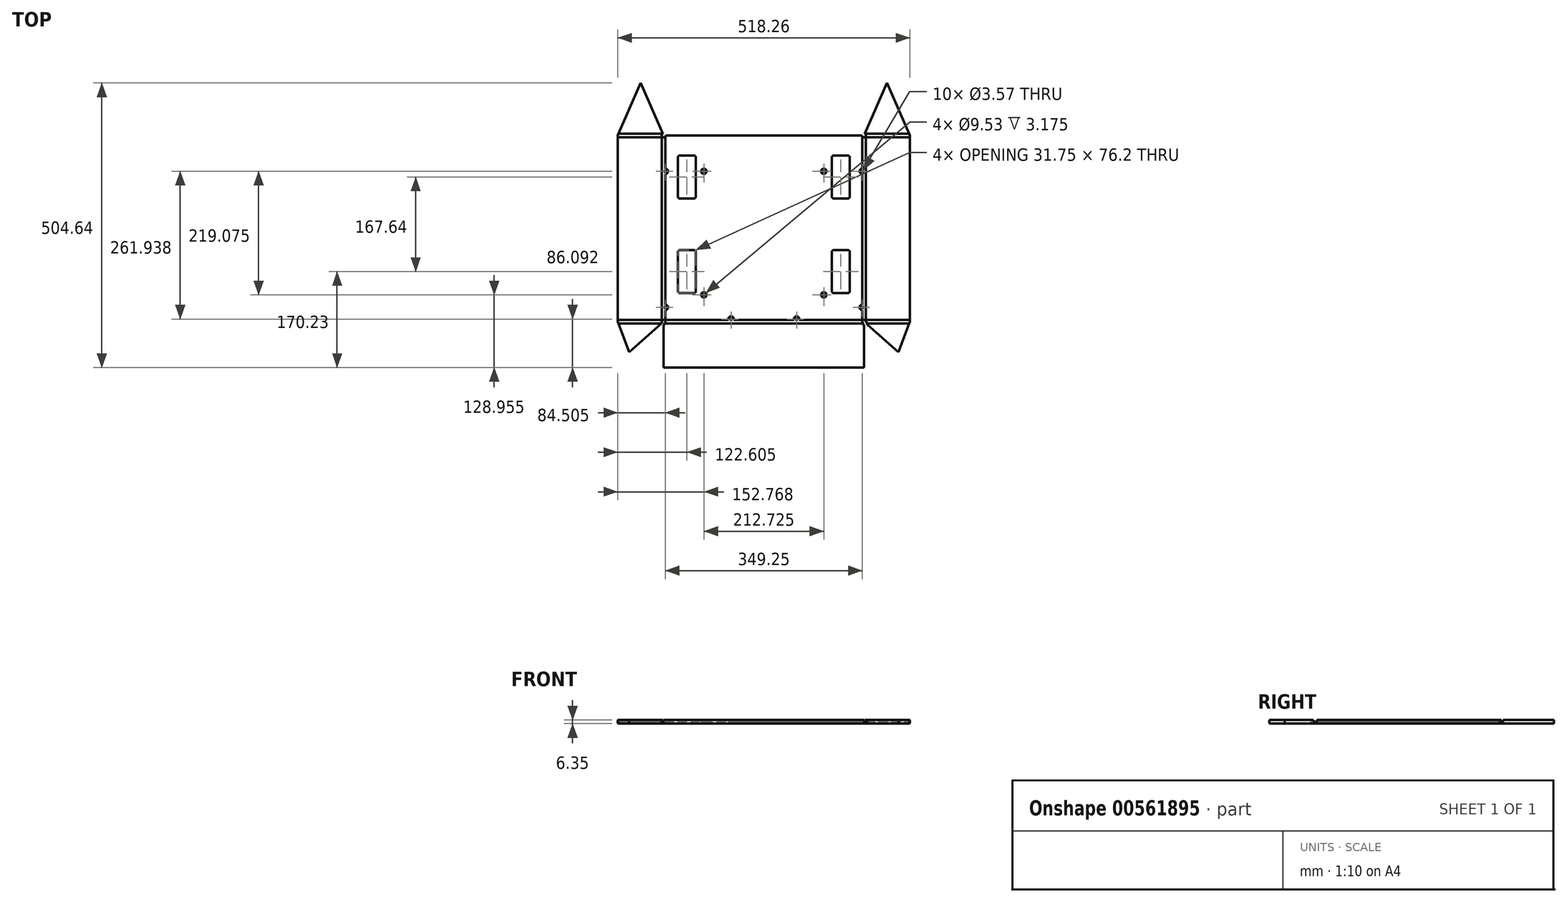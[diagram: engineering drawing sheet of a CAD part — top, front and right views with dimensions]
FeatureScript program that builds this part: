
annotation { "Feature Type Name" : "Feature", "Feature Type Description" : "" }
export const myFeature = defineFeature(function(context is Context, id is Id, definition is map)
    precondition{}
    {
        {
            var Q0;
            Q0=qCreatedBy(makeId("Top.planeOp"),FACE);
            var sketch = newSketch(context, id + "F0", { "sketchPlane" : qUnion([Q0])});
            skLineSegment(sketch, "E0", {"start": v(-255.4, 111.76) * mm, "end": v(-255.4, -218.44) * mm});
            skLineSegment(sketch, "E1", {"start": v(-255.4, -218.44) * mm, "end": v(-234.78, -272.56) * mm});
            skLineSegment(sketch, "E2", {"start": v(-234.78, -272.56) * mm, "end": v(-174.07, -218.44) * mm});
            skLineSegment(sketch, "E3", {"start": v(-174.07, -218.44) * mm, "end": v(-174.07, -299.77) * mm});
            skLineSegment(sketch, "E4", {"start": v(-174.07, -218.44) * mm, "end": v(-174.07, 111.76) * mm, "construction": true});
            skLineSegment(sketch, "E5", {"start": v(-174.07, -218.44) * mm, "end": v(-255.4, -218.44) * mm, "construction": true});
            skLineSegment(sketch, "E6", {"start": v(-174.07, -299.77) * mm, "end": v(181.53, -299.77) * mm});
            skLineSegment(sketch, "E7", {"start": v(181.53, -299.77) * mm, "end": v(181.53, -218.44) * mm});
            skLineSegment(sketch, "E8", {"start": v(181.53, -218.44) * mm, "end": v(242.24, -272.56) * mm});
            skLineSegment(sketch, "E9", {"start": v(242.24, -272.56) * mm, "end": v(262.86, -218.44) * mm});
            skLineSegment(sketch, "E10", {"start": v(181.53, -218.44) * mm, "end": v(262.86, -218.44) * mm, "construction": true});
            skLineSegment(sketch, "E11", {"start": v(-174.07, 111.76) * mm, "end": v(-255.4, 111.76) * mm, "construction": true});
            skLineSegment(sketch, "E12", {"start": v(262.86, -218.44) * mm, "end": v(262.86, 111.76) * mm});
            skLineSegment(sketch, "E13", {"start": v(262.86, 111.76) * mm, "end": v(181.53, 111.76) * mm, "construction": true});
            skLineSegment(sketch, "E14", {"start": v(181.53, 111.76) * mm, "end": v(181.53, -218.44) * mm, "construction": true});
            skLineSegment(sketch, "E15", {"start": v(-255.4, 111.76) * mm, "end": v(-214.74, 204.87) * mm});
            skLineSegment(sketch, "E16", {"start": v(-214.74, 204.87) * mm, "end": v(-174.07, 111.76) * mm});
            skLineSegment(sketch, "E17", {"start": v(181.53, 111.76) * mm, "end": v(222.2, 204.87) * mm});
            skLineSegment(sketch, "E18", {"start": v(222.2, 204.87) * mm, "end": v(262.86, 111.76) * mm});
            skCircle(sketch, "E19", {"center": v(-174.07, -218.44) * mm, "radius": 3.18 * mm});
            skLineSegment(sketch, "E20", {"start": v(-174.62, -215.31) * mm, "end": v(-177.5, -221.5) * mm});
            skLineSegment(sketch, "E21", {"start": v(-171.2, -219.78) * mm, "end": v(-174.07, -225.97) * mm});
            skCircle(sketch, "E22", {"center": v(181.53, -218.44) * mm, "radius": 3.18 * mm});
            skLineSegment(sketch, "E23", {"start": v(178.63, -219.74) * mm, "end": v(181.53, -226.2) * mm});
            skLineSegment(sketch, "E24", {"start": v(184.43, -217.14) * mm, "end": v(187.32, -223.6) * mm});
            skLineSegment(sketch, "E25", {"start": v(-174.07, 111.76) * mm, "end": v(181.53, 111.76) * mm});
            skCircle(sketch, "E26", {"center": v(-174.07, 111.76) * mm, "radius": 3.18 * mm});
            skLineSegment(sketch, "E27", {"start": v(-171.41, 110.02) * mm, "end": v(-170.28, 111.76) * mm});
            skLineSegment(sketch, "E28", {"start": v(-176.73, 113.5) * mm, "end": v(-175.59, 115.24) * mm});
            skCircle(sketch, "E29", {"center": v(181.53, 111.76) * mm, "radius": 3.18 * mm});
            skLineSegment(sketch, "E30", {"start": v(178.87, 110.02) * mm, "end": v(177.74, 111.76) * mm});
            skLineSegment(sketch, "E31", {"start": v(184.19, 113.5) * mm, "end": v(183.05, 115.24) * mm});
            skLineSegment(sketch, "E32", {"start": v(-174.07, -218.44) * mm, "end": v(181.53, -218.44) * mm, "construction": true});
            skLineSegment(sketch, "E33", {"start": v(-148.67, 111.76) * mm, "end": v(-148.67, -218.44) * mm, "construction": true});
            skLineSegment(sketch, "E34", {"start": v(156.13, 111.76) * mm, "end": v(156.13, -218.44) * mm, "construction": true});
            skLineSegment(sketch, "E35", {"start": v(-116.92, 111.76) * mm, "end": v(-116.92, -218.44) * mm, "construction": true});
            skLineSegment(sketch, "E36", {"start": v(124.38, 111.76) * mm, "end": v(124.38, -218.44) * mm, "construction": true});
            skLineSegment(sketch, "E37", {"start": v(-174.07, 76.2) * mm, "end": v(181.53, 76.2) * mm, "construction": true});
            skLineSegment(sketch, "E38", {"start": v(-174.07, 0) * mm, "end": v(181.53, 0) * mm, "construction": true});
            skLineSegment(sketch, "E39", {"start": v(-174.07, -167.64) * mm, "end": v(181.53, -167.64) * mm, "construction": true});
            skLineSegment(sketch, "E40", {"start": v(-174.07, -91.44) * mm, "end": v(181.53, -91.44) * mm, "construction": true});
            skLineSegment(sketch, "E41.bottom", {"start": v(-148.67, 76.2) * mm, "end": v(-116.92, 76.2) * mm});
            skLineSegment(sketch, "E41.top", {"start": v(-148.67, 0) * mm, "end": v(-116.92, 0) * mm});
            skLineSegment(sketch, "E41.left", {"start": v(-148.67, 76.2) * mm, "end": v(-148.67, 0) * mm});
            skLineSegment(sketch, "E41.right", {"start": v(-116.92, 76.2) * mm, "end": v(-116.92, 0) * mm});
            skLineSegment(sketch, "E42.bottom", {"start": v(124.38, 76.2) * mm, "end": v(156.13, 76.2) * mm});
            skLineSegment(sketch, "E42.top", {"start": v(124.38, 0) * mm, "end": v(156.13, 0) * mm});
            skLineSegment(sketch, "E42.left", {"start": v(124.38, 76.2) * mm, "end": v(124.38, 0) * mm});
            skLineSegment(sketch, "E42.right", {"start": v(156.13, 76.2) * mm, "end": v(156.13, 0) * mm});
            skLineSegment(sketch, "E43.bottom", {"start": v(156.13, -91.44) * mm, "end": v(124.38, -91.44) * mm});
            skLineSegment(sketch, "E43.top", {"start": v(156.13, -167.64) * mm, "end": v(124.38, -167.64) * mm});
            skLineSegment(sketch, "E43.left", {"start": v(156.13, -91.44) * mm, "end": v(156.13, -167.64) * mm});
            skLineSegment(sketch, "E43.right", {"start": v(124.38, -91.44) * mm, "end": v(124.38, -167.64) * mm});
            skLineSegment(sketch, "E44.bottom", {"start": v(-116.92, -91.44) * mm, "end": v(-148.67, -91.44) * mm});
            skLineSegment(sketch, "E44.top", {"start": v(-116.92, -167.64) * mm, "end": v(-148.67, -167.64) * mm});
            skLineSegment(sketch, "E44.left", {"start": v(-116.92, -91.44) * mm, "end": v(-116.92, -167.64) * mm});
            skLineSegment(sketch, "E44.right", {"start": v(-148.67, -91.44) * mm, "end": v(-148.67, -167.64) * mm});
            skLineSegment(sketch, "E45", {"start": v(-170.9, 111.76) * mm, "end": v(-170.9, 48.26) * mm, "construction": true});
            skLineSegment(sketch, "E46", {"start": v(-170.9, -218.44) * mm, "end": v(-170.9, -193.04) * mm, "construction": true});
            skLineSegment(sketch, "E47", {"start": v(178.36, -218.44) * mm, "end": v(178.36, -193.04) * mm, "construction": true});
            skLineSegment(sketch, "E48", {"start": v(178.36, 111.76) * mm, "end": v(178.36, 48.26) * mm, "construction": true});
            skLineSegment(sketch, "E49", {"start": v(178.36, 48.26) * mm, "end": v(110.1, 48.26) * mm, "construction": true});
            skLineSegment(sketch, "E50", {"start": v(-170.9, 48.26) * mm, "end": v(-102.63, 48.26) * mm, "construction": true});
            skPoint(sketch, "E51", {"position": v(-102.63, 48.26) * mm});
            skPoint(sketch, "E52", {"position": v(-102.63, -170.82) * mm});
            skPoint(sketch, "E53", {"position": v(110.1, -170.81) * mm});
            skPoint(sketch, "E54", {"position": v(110.1, 48.26) * mm});
            skLineSegment(sketch, "E55", {"start": v(-174.07, -213.68) * mm, "end": v(181.53, -213.68) * mm, "construction": true});
            skPoint(sketch, "E56", {"position": v(61.83, -213.68) * mm});
            skPoint(sketch, "E57", {"position": v(-54.37, -213.68) * mm});
            skLineSegment(sketch, "E58", {"start": v(-102.63, -170.82) * mm, "end": v(-102.63, -218.44) * mm, "construction": true});
            skLineSegment(sketch, "E59", {"start": v(110.1, -170.81) * mm, "end": v(110.1, -218.44) * mm, "construction": true});
            skSolve(sketch);
        }
        {
            var Q0;
            Q0=makeQuery(id+"F0.imprint","IMPRINT",FACE,{"disambiguationData":[TD([[makeQuery(id+"F0.imprint","IMPRINT",EDGE,{"derivedFrom":sQuery(id+"F0.wireOp",EDGE,"E0")}),1.0]])]});
            extrude(context, id + "F1", {"entities" : qUnion([Q0]), "depth" : 6.35 * mm});
        }
        {
            var Q0;
            Q0=makeQuery(id+"F1.opExtrude","SWEPT_EDGE",EDGE,{"disambiguationData":[OSD([sQuery(id+"F0.wireOp",EDGE,"E42.bottom"),sQuery(id+"F0.wireOp",EDGE,"E42.right")])]});
            var Q1;
            Q1=makeQuery(id+"F1.opExtrude","SWEPT_EDGE",EDGE,{"disambiguationData":[OSD([sQuery(id+"F0.wireOp",EDGE,"E42.bottom"),sQuery(id+"F0.wireOp",EDGE,"E42.left")])]});
            var Q2;
            Q2=makeQuery(id+"F1.opExtrude","SWEPT_EDGE",EDGE,{"disambiguationData":[OSD([sQuery(id+"F0.wireOp",EDGE,"E42.top"),sQuery(id+"F0.wireOp",EDGE,"E42.left")])]});
            var Q3;
            Q3=makeQuery(id+"F1.opExtrude","SWEPT_EDGE",EDGE,{"disambiguationData":[OSD([sQuery(id+"F0.wireOp",EDGE,"E42.top"),sQuery(id+"F0.wireOp",EDGE,"E42.right")])]});
            var Q4;
            Q4=makeQuery(id+"F1.opExtrude","SWEPT_EDGE",EDGE,{"disambiguationData":[OSD([sQuery(id+"F0.wireOp",EDGE,"E43.top"),sQuery(id+"F0.wireOp",EDGE,"E43.left")])]});
            var Q5;
            Q5=makeQuery(id+"F1.opExtrude","SWEPT_EDGE",EDGE,{"disambiguationData":[OSD([sQuery(id+"F0.wireOp",EDGE,"E43.top"),sQuery(id+"F0.wireOp",EDGE,"E43.right")])]});
            var Q6;
            Q6=makeQuery(id+"F1.opExtrude","SWEPT_EDGE",EDGE,{"disambiguationData":[OSD([sQuery(id+"F0.wireOp",EDGE,"E43.bottom"),sQuery(id+"F0.wireOp",EDGE,"E43.right")])]});
            var Q7;
            Q7=makeQuery(id+"F1.opExtrude","SWEPT_EDGE",EDGE,{"disambiguationData":[OSD([sQuery(id+"F0.wireOp",EDGE,"E43.bottom"),sQuery(id+"F0.wireOp",EDGE,"E43.left")])]});
            var Q8;
            Q8=makeQuery(id+"F1.opExtrude","SWEPT_EDGE",EDGE,{"disambiguationData":[OSD([sQuery(id+"F0.wireOp",EDGE,"E44.bottom"),sQuery(id+"F0.wireOp",EDGE,"E44.left")])]});
            var Q9;
            Q9=makeQuery(id+"F1.opExtrude","SWEPT_EDGE",EDGE,{"disambiguationData":[OSD([sQuery(id+"F0.wireOp",EDGE,"E44.top"),sQuery(id+"F0.wireOp",EDGE,"E44.left")])]});
            var Q10;
            Q10=makeQuery(id+"F1.opExtrude","SWEPT_EDGE",EDGE,{"disambiguationData":[OSD([sQuery(id+"F0.wireOp",EDGE,"E41.top"),sQuery(id+"F0.wireOp",EDGE,"E41.right")])]});
            var Q11;
            Q11=makeQuery(id+"F1.opExtrude","SWEPT_EDGE",EDGE,{"disambiguationData":[OSD([sQuery(id+"F0.wireOp",EDGE,"E44.top"),sQuery(id+"F0.wireOp",EDGE,"E44.right")])]});
            var Q12;
            Q12=makeQuery(id+"F1.opExtrude","SWEPT_EDGE",EDGE,{"disambiguationData":[OSD([sQuery(id+"F0.wireOp",EDGE,"E41.top"),sQuery(id+"F0.wireOp",EDGE,"E41.left")])]});
            var Q13;
            Q13=makeQuery(id+"F1.opExtrude","SWEPT_EDGE",EDGE,{"disambiguationData":[OSD([sQuery(id+"F0.wireOp",EDGE,"E44.bottom"),sQuery(id+"F0.wireOp",EDGE,"E44.right")])]});
            var Q14;
            Q14=makeQuery(id+"F1.opExtrude","SWEPT_EDGE",EDGE,{"disambiguationData":[OSD([sQuery(id+"F0.wireOp",EDGE,"E41.bottom"),sQuery(id+"F0.wireOp",EDGE,"E41.left")])]});
            var Q15;
            Q15=makeQuery(id+"F1.opExtrude","SWEPT_EDGE",EDGE,{"disambiguationData":[OSD([sQuery(id+"F0.wireOp",EDGE,"E41.bottom"),sQuery(id+"F0.wireOp",EDGE,"E41.right")])]});
            fillet(context, id + "F2", {"entities" : qUnion([Q0, Q1, Q2, Q3, Q4, Q5, Q6, Q7, Q8, Q9, Q10, Q11, Q12, Q13, Q14, Q15]), "radius" : 3.17 * mm, "tangentPropagation" : true, "allowEdgeOverflow" : false});
        }
        {
            var Q0;
            Q0=sQuery(id+"F0.wireOp",VERTEX,"E48.end");
            var Q1;
            Q1=makeQuery(id+"F1.opExtrude","SWEPT_BODY",BODY,{"disambiguationData":[OSD([sQuery(id+"F0.wireOp",EDGE,"E0"),sQuery(id+"F0.wireOp",EDGE,"E1"),sQuery(id+"F0.wireOp",EDGE,"E2"),sQuery(id+"F0.wireOp",EDGE,"E3"),sQuery(id+"F0.wireOp",EDGE,"E6"),sQuery(id+"F0.wireOp",EDGE,"E7"),sQuery(id+"F0.wireOp",EDGE,"E8"),sQuery(id+"F0.wireOp",EDGE,"E9"),sQuery(id+"F0.wireOp",EDGE,"E12"),sQuery(id+"F0.wireOp",EDGE,"E15"),sQuery(id+"F0.wireOp",EDGE,"E16"),sQuery(id+"F0.wireOp",EDGE,"E17"),sQuery(id+"F0.wireOp",EDGE,"E18"),sQuery(id+"F0.wireOp",EDGE,"E19"),sQuery(id+"F0.wireOp",EDGE,"E20"),sQuery(id+"F0.wireOp",EDGE,"E21"),sQuery(id+"F0.wireOp",EDGE,"E22"),sQuery(id+"F0.wireOp",EDGE,"E23"),sQuery(id+"F0.wireOp",EDGE,"E24"),sQuery(id+"F0.wireOp",EDGE,"E25"),sQuery(id+"F0.wireOp",EDGE,"E26"),sQuery(id+"F0.wireOp",EDGE,"E27"),sQuery(id+"F0.wireOp",EDGE,"E28"),sQuery(id+"F0.wireOp",EDGE,"E29"),sQuery(id+"F0.wireOp",EDGE,"E30"),sQuery(id+"F0.wireOp",EDGE,"E31"),sQuery(id+"F0.wireOp",EDGE,"E41.bottom"),sQuery(id+"F0.wireOp",EDGE,"E41.top"),sQuery(id+"F0.wireOp",EDGE,"E41.left"),sQuery(id+"F0.wireOp",EDGE,"E41.right"),sQuery(id+"F0.wireOp",EDGE,"E42.bottom"),sQuery(id+"F0.wireOp",EDGE,"E42.top"),sQuery(id+"F0.wireOp",EDGE,"E42.left"),sQuery(id+"F0.wireOp",EDGE,"E42.right"),sQuery(id+"F0.wireOp",EDGE,"E43.bottom"),sQuery(id+"F0.wireOp",EDGE,"E43.top"),sQuery(id+"F0.wireOp",EDGE,"E43.left"),sQuery(id+"F0.wireOp",EDGE,"E43.right"),sQuery(id+"F0.wireOp",EDGE,"E44.bottom"),sQuery(id+"F0.wireOp",EDGE,"E44.top"),sQuery(id+"F0.wireOp",EDGE,"E44.left"),sQuery(id+"F0.wireOp",EDGE,"E44.right")])]});
            hole(context, id + "F3", {"style" : HoleStyle.SIMPLE, "endStyle" : HoleEndStyle.BLIND, "oppositeDirection" : true, "holeDiameter" : 3.57 * mm, "majorDiameter" : 6.35 * mm, "holeDepth" : 6.35 * mm, "isTappedThrough" : true, "tappedDepth" : 12.7 * mm, "tapClearance" : 3, "startFromSketch" : true, "locations" : qUnion([Q0]), "scope" : qUnion([Q1])});
        }
        {
            var Q0;
            Q0=sQuery(id+"F0.wireOp",VERTEX,"E47.end");
            var Q1;
            Q1=makeQuery(id+"F1.opExtrude","SWEPT_BODY",BODY,{"disambiguationData":[OSD([sQuery(id+"F0.wireOp",EDGE,"E0"),sQuery(id+"F0.wireOp",EDGE,"E1"),sQuery(id+"F0.wireOp",EDGE,"E2"),sQuery(id+"F0.wireOp",EDGE,"E3"),sQuery(id+"F0.wireOp",EDGE,"E6"),sQuery(id+"F0.wireOp",EDGE,"E7"),sQuery(id+"F0.wireOp",EDGE,"E8"),sQuery(id+"F0.wireOp",EDGE,"E9"),sQuery(id+"F0.wireOp",EDGE,"E12"),sQuery(id+"F0.wireOp",EDGE,"E15"),sQuery(id+"F0.wireOp",EDGE,"E16"),sQuery(id+"F0.wireOp",EDGE,"E17"),sQuery(id+"F0.wireOp",EDGE,"E18"),sQuery(id+"F0.wireOp",EDGE,"E19"),sQuery(id+"F0.wireOp",EDGE,"E20"),sQuery(id+"F0.wireOp",EDGE,"E21"),sQuery(id+"F0.wireOp",EDGE,"E22"),sQuery(id+"F0.wireOp",EDGE,"E23"),sQuery(id+"F0.wireOp",EDGE,"E24"),sQuery(id+"F0.wireOp",EDGE,"E25"),sQuery(id+"F0.wireOp",EDGE,"E26"),sQuery(id+"F0.wireOp",EDGE,"E27"),sQuery(id+"F0.wireOp",EDGE,"E28"),sQuery(id+"F0.wireOp",EDGE,"E29"),sQuery(id+"F0.wireOp",EDGE,"E30"),sQuery(id+"F0.wireOp",EDGE,"E31"),sQuery(id+"F0.wireOp",EDGE,"E41.bottom"),sQuery(id+"F0.wireOp",EDGE,"E41.top"),sQuery(id+"F0.wireOp",EDGE,"E41.left"),sQuery(id+"F0.wireOp",EDGE,"E41.right"),sQuery(id+"F0.wireOp",EDGE,"E42.bottom"),sQuery(id+"F0.wireOp",EDGE,"E42.top"),sQuery(id+"F0.wireOp",EDGE,"E42.left"),sQuery(id+"F0.wireOp",EDGE,"E42.right"),sQuery(id+"F0.wireOp",EDGE,"E43.bottom"),sQuery(id+"F0.wireOp",EDGE,"E43.top"),sQuery(id+"F0.wireOp",EDGE,"E43.left"),sQuery(id+"F0.wireOp",EDGE,"E43.right"),sQuery(id+"F0.wireOp",EDGE,"E44.bottom"),sQuery(id+"F0.wireOp",EDGE,"E44.top"),sQuery(id+"F0.wireOp",EDGE,"E44.left"),sQuery(id+"F0.wireOp",EDGE,"E44.right")])]});
            hole(context, id + "F4", {"style" : HoleStyle.SIMPLE, "endStyle" : HoleEndStyle.BLIND, "oppositeDirection" : true, "holeDiameter" : 3.57 * mm, "majorDiameter" : 6.35 * mm, "holeDepth" : 6.35 * mm, "isTappedThrough" : true, "tappedDepth" : 12.7 * mm, "tapClearance" : 3, "startFromSketch" : true, "locations" : qUnion([Q0]), "scope" : qUnion([Q1])});
        }
        {
            var Q0;
            Q0=sQuery(id+"F0.wireOp",VERTEX,"E46.end");
            var Q1;
            Q1=makeQuery(id+"F1.opExtrude","SWEPT_BODY",BODY,{"disambiguationData":[OSD([sQuery(id+"F0.wireOp",EDGE,"E0"),sQuery(id+"F0.wireOp",EDGE,"E1"),sQuery(id+"F0.wireOp",EDGE,"E2"),sQuery(id+"F0.wireOp",EDGE,"E3"),sQuery(id+"F0.wireOp",EDGE,"E6"),sQuery(id+"F0.wireOp",EDGE,"E7"),sQuery(id+"F0.wireOp",EDGE,"E8"),sQuery(id+"F0.wireOp",EDGE,"E9"),sQuery(id+"F0.wireOp",EDGE,"E12"),sQuery(id+"F0.wireOp",EDGE,"E15"),sQuery(id+"F0.wireOp",EDGE,"E16"),sQuery(id+"F0.wireOp",EDGE,"E17"),sQuery(id+"F0.wireOp",EDGE,"E18"),sQuery(id+"F0.wireOp",EDGE,"E19"),sQuery(id+"F0.wireOp",EDGE,"E20"),sQuery(id+"F0.wireOp",EDGE,"E21"),sQuery(id+"F0.wireOp",EDGE,"E22"),sQuery(id+"F0.wireOp",EDGE,"E23"),sQuery(id+"F0.wireOp",EDGE,"E24"),sQuery(id+"F0.wireOp",EDGE,"E25"),sQuery(id+"F0.wireOp",EDGE,"E26"),sQuery(id+"F0.wireOp",EDGE,"E27"),sQuery(id+"F0.wireOp",EDGE,"E28"),sQuery(id+"F0.wireOp",EDGE,"E29"),sQuery(id+"F0.wireOp",EDGE,"E30"),sQuery(id+"F0.wireOp",EDGE,"E31"),sQuery(id+"F0.wireOp",EDGE,"E41.bottom"),sQuery(id+"F0.wireOp",EDGE,"E41.top"),sQuery(id+"F0.wireOp",EDGE,"E41.left"),sQuery(id+"F0.wireOp",EDGE,"E41.right"),sQuery(id+"F0.wireOp",EDGE,"E42.bottom"),sQuery(id+"F0.wireOp",EDGE,"E42.top"),sQuery(id+"F0.wireOp",EDGE,"E42.left"),sQuery(id+"F0.wireOp",EDGE,"E42.right"),sQuery(id+"F0.wireOp",EDGE,"E43.bottom"),sQuery(id+"F0.wireOp",EDGE,"E43.top"),sQuery(id+"F0.wireOp",EDGE,"E43.left"),sQuery(id+"F0.wireOp",EDGE,"E43.right"),sQuery(id+"F0.wireOp",EDGE,"E44.bottom"),sQuery(id+"F0.wireOp",EDGE,"E44.top"),sQuery(id+"F0.wireOp",EDGE,"E44.left"),sQuery(id+"F0.wireOp",EDGE,"E44.right")])]});
            hole(context, id + "F5", {"style" : HoleStyle.SIMPLE, "endStyle" : HoleEndStyle.BLIND, "oppositeDirection" : true, "holeDiameter" : 3.57 * mm, "majorDiameter" : 6.35 * mm, "holeDepth" : 6.35 * mm, "isTappedThrough" : true, "tappedDepth" : 12.7 * mm, "tapClearance" : 3, "startFromSketch" : true, "locations" : qUnion([Q0]), "scope" : qUnion([Q1])});
        }
        {
            var Q0;
            Q0=sQuery(id+"F0.wireOp",VERTEX,"E45.end");
            var Q1;
            Q1=sQuery(id+"F0.wireOp",VERTEX,"E51");
            var Q2;
            Q2=sQuery(id+"F0.wireOp",VERTEX,"E54");
            var Q3;
            Q3=sQuery(id+"F0.wireOp",VERTEX,"E53");
            var Q4;
            Q4=sQuery(id+"F0.wireOp",VERTEX,"E52");
            var Q5;
            Q5=sQuery(id+"F0.wireOp",VERTEX,"E57");
            var Q6;
            Q6=sQuery(id+"F0.wireOp",VERTEX,"E56");
            var Q7;
            Q7=makeQuery(id+"F1.opExtrude","SWEPT_BODY",BODY,{"disambiguationData":[OSD([sQuery(id+"F0.wireOp",EDGE,"E0"),sQuery(id+"F0.wireOp",EDGE,"E1"),sQuery(id+"F0.wireOp",EDGE,"E2"),sQuery(id+"F0.wireOp",EDGE,"E3"),sQuery(id+"F0.wireOp",EDGE,"E6"),sQuery(id+"F0.wireOp",EDGE,"E7"),sQuery(id+"F0.wireOp",EDGE,"E8"),sQuery(id+"F0.wireOp",EDGE,"E9"),sQuery(id+"F0.wireOp",EDGE,"E12"),sQuery(id+"F0.wireOp",EDGE,"E15"),sQuery(id+"F0.wireOp",EDGE,"E16"),sQuery(id+"F0.wireOp",EDGE,"E17"),sQuery(id+"F0.wireOp",EDGE,"E18"),sQuery(id+"F0.wireOp",EDGE,"E19"),sQuery(id+"F0.wireOp",EDGE,"E20"),sQuery(id+"F0.wireOp",EDGE,"E21"),sQuery(id+"F0.wireOp",EDGE,"E22"),sQuery(id+"F0.wireOp",EDGE,"E23"),sQuery(id+"F0.wireOp",EDGE,"E24"),sQuery(id+"F0.wireOp",EDGE,"E25"),sQuery(id+"F0.wireOp",EDGE,"E26"),sQuery(id+"F0.wireOp",EDGE,"E27"),sQuery(id+"F0.wireOp",EDGE,"E28"),sQuery(id+"F0.wireOp",EDGE,"E29"),sQuery(id+"F0.wireOp",EDGE,"E30"),sQuery(id+"F0.wireOp",EDGE,"E31"),sQuery(id+"F0.wireOp",EDGE,"E41.bottom"),sQuery(id+"F0.wireOp",EDGE,"E41.top"),sQuery(id+"F0.wireOp",EDGE,"E41.left"),sQuery(id+"F0.wireOp",EDGE,"E41.right"),sQuery(id+"F0.wireOp",EDGE,"E42.bottom"),sQuery(id+"F0.wireOp",EDGE,"E42.top"),sQuery(id+"F0.wireOp",EDGE,"E42.left"),sQuery(id+"F0.wireOp",EDGE,"E42.right"),sQuery(id+"F0.wireOp",EDGE,"E43.bottom"),sQuery(id+"F0.wireOp",EDGE,"E43.top"),sQuery(id+"F0.wireOp",EDGE,"E43.left"),sQuery(id+"F0.wireOp",EDGE,"E43.right"),sQuery(id+"F0.wireOp",EDGE,"E44.bottom"),sQuery(id+"F0.wireOp",EDGE,"E44.top"),sQuery(id+"F0.wireOp",EDGE,"E44.left"),sQuery(id+"F0.wireOp",EDGE,"E44.right")])]});
            hole(context, id + "F6", {"style" : HoleStyle.SIMPLE, "endStyle" : HoleEndStyle.BLIND, "oppositeDirection" : true, "holeDiameter" : 3.57 * mm, "majorDiameter" : 6.35 * mm, "holeDepth" : 6.35 * mm, "isTappedThrough" : true, "tappedDepth" : 12.7 * mm, "tapClearance" : 3, "startFromSketch" : true, "locations" : qUnion([Q0, Q1, Q2, Q3, Q4, Q5, Q6]), "scope" : qUnion([Q7])});
        }
        {
            var Q0;
            Q0=makeQuery(id+"F1.opExtrude","CAP_FACE",FACE,{"disambiguationData":[OSD([sQuery(id+"F0.wireOp",EDGE,"E0"),sQuery(id+"F0.wireOp",EDGE,"E1"),sQuery(id+"F0.wireOp",EDGE,"E2"),sQuery(id+"F0.wireOp",EDGE,"E3"),sQuery(id+"F0.wireOp",EDGE,"E6"),sQuery(id+"F0.wireOp",EDGE,"E7"),sQuery(id+"F0.wireOp",EDGE,"E8"),sQuery(id+"F0.wireOp",EDGE,"E9"),sQuery(id+"F0.wireOp",EDGE,"E12"),sQuery(id+"F0.wireOp",EDGE,"E15"),sQuery(id+"F0.wireOp",EDGE,"E16"),sQuery(id+"F0.wireOp",EDGE,"E17"),sQuery(id+"F0.wireOp",EDGE,"E18"),sQuery(id+"F0.wireOp",EDGE,"E19"),sQuery(id+"F0.wireOp",EDGE,"E20"),sQuery(id+"F0.wireOp",EDGE,"E21"),sQuery(id+"F0.wireOp",EDGE,"E22"),sQuery(id+"F0.wireOp",EDGE,"E23"),sQuery(id+"F0.wireOp",EDGE,"E24"),sQuery(id+"F0.wireOp",EDGE,"E25"),sQuery(id+"F0.wireOp",EDGE,"E26"),sQuery(id+"F0.wireOp",EDGE,"E27"),sQuery(id+"F0.wireOp",EDGE,"E28"),sQuery(id+"F0.wireOp",EDGE,"E29"),sQuery(id+"F0.wireOp",EDGE,"E30"),sQuery(id+"F0.wireOp",EDGE,"E31"),sQuery(id+"F0.wireOp",EDGE,"E41.bottom"),sQuery(id+"F0.wireOp",EDGE,"E41.top"),sQuery(id+"F0.wireOp",EDGE,"E41.left"),sQuery(id+"F0.wireOp",EDGE,"E41.right"),sQuery(id+"F0.wireOp",EDGE,"E42.bottom"),sQuery(id+"F0.wireOp",EDGE,"E42.top"),sQuery(id+"F0.wireOp",EDGE,"E42.left"),sQuery(id+"F0.wireOp",EDGE,"E42.right"),sQuery(id+"F0.wireOp",EDGE,"E43.bottom"),sQuery(id+"F0.wireOp",EDGE,"E43.top"),sQuery(id+"F0.wireOp",EDGE,"E43.left"),sQuery(id+"F0.wireOp",EDGE,"E43.right"),sQuery(id+"F0.wireOp",EDGE,"E44.bottom"),sQuery(id+"F0.wireOp",EDGE,"E44.top"),sQuery(id+"F0.wireOp",EDGE,"E44.left"),sQuery(id+"F0.wireOp",EDGE,"E44.right")])],"isStart":false});
            var sketch = newSketch(context, id + "F7", { "sketchPlane" : qUnion([Q0])});
            skCircle(sketch, "E60", {"center": v(-170.9, -193.04) * mm, "radius": 3.17 * mm});
            skCircle(sketch, "E61", {"center": v(-170.9, 48.26) * mm, "radius": 3.18 * mm});
            skSolve(sketch);
        }
        {
            var Q0;
            Q0=makeQuery(id+"F7.imprint","IMPRINT",FACE,{"disambiguationData":[TD([[makeQuery(id+"F7.imprint","IMPRINT",EDGE,{"derivedFrom":sQuery(id+"F7.wireOp",EDGE,"E60")}),-1.0]])]});
            var sketch = newSketch(context, id + "F8", { "sketchPlane" : qUnion([Q0])});
            skLineSegment(sketch, "E62", {"start": v(-170.9, -218.44) * mm, "end": v(-170.9, 111.76) * mm});
            skLineSegment(sketch, "E63", {"start": v(-177.24, 111.76) * mm, "end": v(-177.24, -218.44) * mm});
            skLineSegment(sketch, "E64", {"start": v(-174.07, 108.58) * mm, "end": v(-255.4, 108.58) * mm});
            skLineSegment(sketch, "E65", {"start": v(-254.01, 114.93) * mm, "end": v(-174.07, 114.93) * mm});
            skLineSegment(sketch, "E66", {"start": v(-255.4, 108.59) * mm, "end": v(-255.4, 111.76) * mm});
            skLineSegment(sketch, "E67", {"start": v(-255.4, 111.76) * mm, "end": v(-254.01, 114.94) * mm});
            skLineSegment(sketch, "E68", {"start": v(-255.4, -215.27) * mm, "end": v(262.86, -215.27) * mm});
            skLineSegment(sketch, "E69", {"start": v(-254.2, -221.62) * mm, "end": v(261.65, -221.62) * mm});
            skLineSegment(sketch, "E70", {"start": v(-255.4, -215.26) * mm, "end": v(-255.4, -218.44) * mm});
            skLineSegment(sketch, "E71", {"start": v(-255.4, -218.44) * mm, "end": v(-254.2, -221.62) * mm});
            skLineSegment(sketch, "E72", {"start": v(262.86, -215.26) * mm, "end": v(262.86, -218.44) * mm});
            skLineSegment(sketch, "E73", {"start": v(262.86, -218.44) * mm, "end": v(261.65, -221.62) * mm});
            skLineSegment(sketch, "E74", {"start": v(184.7, -218.44) * mm, "end": v(184.7, 111.76) * mm});
            skLineSegment(sketch, "E75", {"start": v(178.36, 111.76) * mm, "end": v(178.36, -218.44) * mm});
            skLineSegment(sketch, "E76", {"start": v(181.53, 114.93) * mm, "end": v(261.47, 114.93) * mm});
            skLineSegment(sketch, "E77", {"start": v(181.53, 108.58) * mm, "end": v(262.86, 108.58) * mm});
            skLineSegment(sketch, "E78", {"start": v(262.86, 108.59) * mm, "end": v(262.86, 111.76) * mm});
            skLineSegment(sketch, "E79", {"start": v(262.86, 111.76) * mm, "end": v(261.47, 114.94) * mm});
            skLineSegment(sketch, "E80", {"start": v(178.36, 111.76) * mm, "end": v(184.7, 111.76) * mm});
            skLineSegment(sketch, "E81", {"start": v(181.53, 108.59) * mm, "end": v(181.53, 114.94) * mm});
            skLineSegment(sketch, "E82", {"start": v(178.36, -218.44) * mm, "end": v(184.7, -218.44) * mm});
            skLineSegment(sketch, "E83", {"start": v(-177.24, -218.44) * mm, "end": v(-170.9, -218.44) * mm});
            skLineSegment(sketch, "E84", {"start": v(-177.24, 111.76) * mm, "end": v(-170.9, 111.76) * mm});
            skLineSegment(sketch, "E85", {"start": v(-174.07, 108.59) * mm, "end": v(-174.07, 114.94) * mm});
            skCircle(sketch, "E86", {"center": v(-170.9, 48.26) * mm, "radius": 4.76 * mm});
            skCircle(sketch, "E87", {"center": v(-170.9, -193.04) * mm, "radius": 4.76 * mm});
            skCircle(sketch, "E88", {"center": v(-102.63, -170.82) * mm, "radius": 4.76 * mm});
            skCircle(sketch, "E89", {"center": v(-102.63, 48.26) * mm, "radius": 4.76 * mm});
            skArc(sketch, "E90", {"start": v(-49.88, -215.27) * mm, "mid": v(-54.37, -208.92) * mm, "end": v(-58.86, -215.27) * mm});
            skArc(sketch, "E91", {"start": v(66.32, -215.27) * mm, "mid": v(61.83, -208.92) * mm, "end": v(57.34, -215.27) * mm});
            skCircle(sketch, "E92", {"center": v(110.1, -170.81) * mm, "radius": 4.76 * mm});
            skCircle(sketch, "E93", {"center": v(178.36, -193.04) * mm, "radius": 4.76 * mm});
            skCircle(sketch, "E94", {"center": v(110.1, 48.26) * mm, "radius": 4.76 * mm});
            skCircle(sketch, "E95", {"center": v(178.36, 48.26) * mm, "radius": 4.76 * mm});
            skLineSegment(sketch, "E96", {"start": v(-59.13, -215.26) * mm, "end": v(-59.13, -213.68) * mm});
            skLineSegment(sketch, "E97", {"start": v(-49.6, -215.26) * mm, "end": v(-49.6, -213.68) * mm});
            skLineSegment(sketch, "E98", {"start": v(57.07, -215.26) * mm, "end": v(57.07, -213.68) * mm});
            skLineSegment(sketch, "E99", {"start": v(66.6, -215.26) * mm, "end": v(66.6, -213.68) * mm});
            skSolve(sketch);
        }
        {
            var Q0;
            Q0 = qSketchRegion(id + "F8", true);
            extrude(context, id + "F9", {"entities" : qUnion([Q0]), "operationType" : NewBodyOperationType.REMOVE, "oppositeDirection" : true, "depth" : 3.17 * mm, "offsetDistance" : 25.4 * mm});
        }
    });
